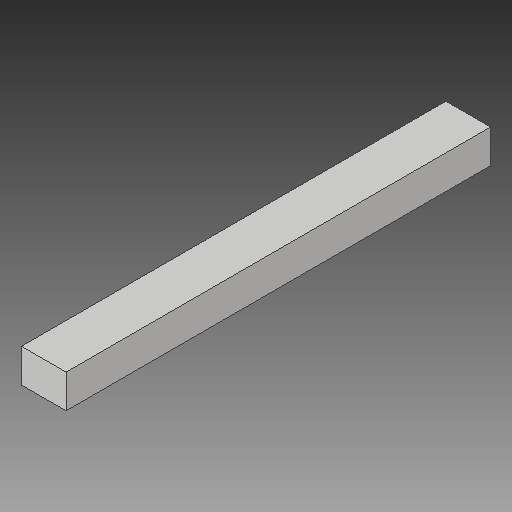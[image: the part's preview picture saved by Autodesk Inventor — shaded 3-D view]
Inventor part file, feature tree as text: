
AUTODESK INVENTOR PART (.ipt)
format: ipt  version: 2017 (Build 210142000, 142)  size: 90,624 bytes
history: native  units: in
note: dims shown in document units (in); Inventor stores cm internally (conversion verified against a paired STEP export)
features: extrude x1, sketch x1
ambient origin geometry x8: Origin, YZ Plane, XZ Plane, XY Plane, X Axis, Y Axis, Z Axis, Center Point
bodies: Solid1 (feature_tree)
feature tree (2):
  extrude  "Extrusion1"  Depth=9.5in
  sketch  "Sketch1"  dims[d0=1.0in d1=9.5in d2=0.75in d3=0.0in]
